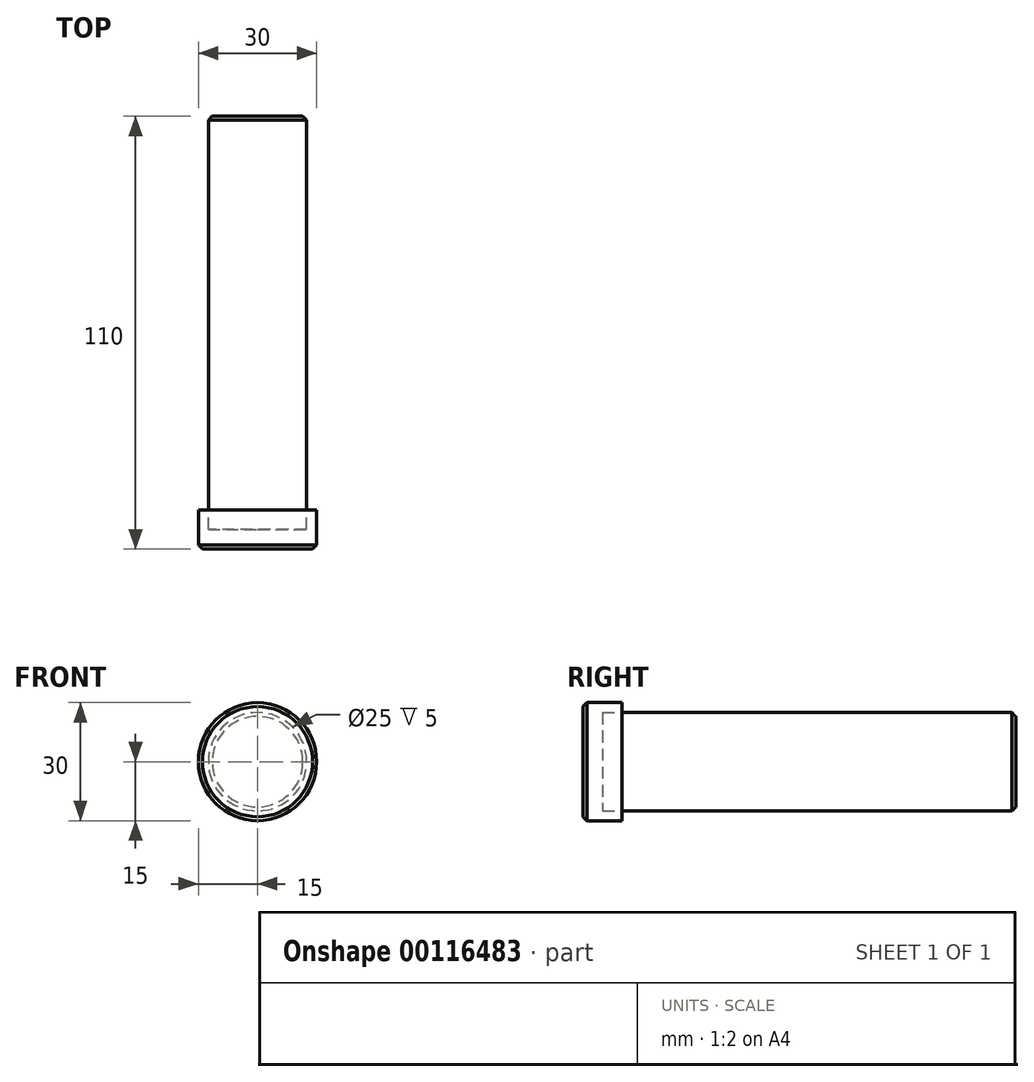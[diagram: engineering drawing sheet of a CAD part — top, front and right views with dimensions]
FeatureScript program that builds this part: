
annotation { "Feature Type Name" : "Feature", "Feature Type Description" : "" }
export const myFeature = defineFeature(function(context is Context, id is Id, definition is map)
    precondition{}
    {
        {
            var Q0;
            Q0=qCreatedBy(makeId("Front.planeOp"),FACE);
            var sketch = newSketch(context, id + "F0", { "sketchPlane" : qUnion([Q0])});
            skCircle(sketch, "E0", {"center": v(0, 0) * mm, "radius": 15 * mm});
            skPoint(sketch, "E1", {"position": v(-2.9, 0) * mm});
            skSolve(sketch);
        }
        {
            var Q0;
            Q0 = qSketchRegion(id + "F0", true);
            var Q1;
            Q1=makeQuery(id+"F0.imprint","IMPRINT",FACE,{"disambiguationData":[TD([[makeQuery(id+"F0.imprint","IMPRINT",EDGE,{"derivedFrom":sQuery(id+"F0.wireOp",EDGE,"E0")}),1.0]])]});
            extrude(context, id + "F1", {"entities" : qUnion([Q0, Q1]), "endBound" : BoundingType.SYMMETRIC, "depth" : 10 * mm});
        }
        {
            var Q0;
            Q0=makeQuery(id+"F1.opExtrude","CAP_EDGE",EDGE,{"disambiguationData":[OSD([sQuery(id+"F0.wireOp",EDGE,"E0")])],"isStart":false});
            chamfer(context, id + "F2", {"entities" : qUnion([Q0]), "width" : 1 * mm, "tangentPropagation" : true});
        }
        {
            var Q0;
            Q0=makeQuery(id+"F1.opExtrude","CAP_FACE",FACE,{"disambiguationData":[OSD([sQuery(id+"F0.wireOp",EDGE,"E0")])],"isStart":true});
            var sketch = newSketch(context, id + "F3", { "sketchPlane" : qUnion([Q0])});
            skCircle(sketch, "E2", {"center": v(0, 0) * mm, "radius": 12.5 * mm});
            skSolve(sketch);
        }
        {
            var Q0;
            Q0 = qSketchRegion(id + "F3", true);
            extrude(context, id + "F4", {"entities" : qUnion([Q0]), "operationType" : NewBodyOperationType.REMOVE, "oppositeDirection" : true, "depth" : 5 * mm});
        }
        {
            var Q0;
            Q0=makeQuery(id+"F3.imprint","IMPRINT",FACE,{"disambiguationData":[TD([[makeQuery(id+"F3.imprint","IMPRINT",EDGE,{"derivedFrom":sQuery(id+"F3.wireOp",EDGE,"E2")}),1.0]])]});
            extrude(context, id + "F5", {"entities" : qUnion([Q0]), "depth" : 100 * mm});
        }
        {
            var Q0;
            Q0=makeQuery(id+"F5.opExtrude","CAP_EDGE",EDGE,{"disambiguationData":[OSD([sQuery(id+"F3.wireOp",EDGE,"E2")])],"isStart":false});
            chamfer(context, id + "F6", {"entities" : qUnion([Q0]), "width" : 1 * mm, "tangentPropagation" : true});
        }
    });
